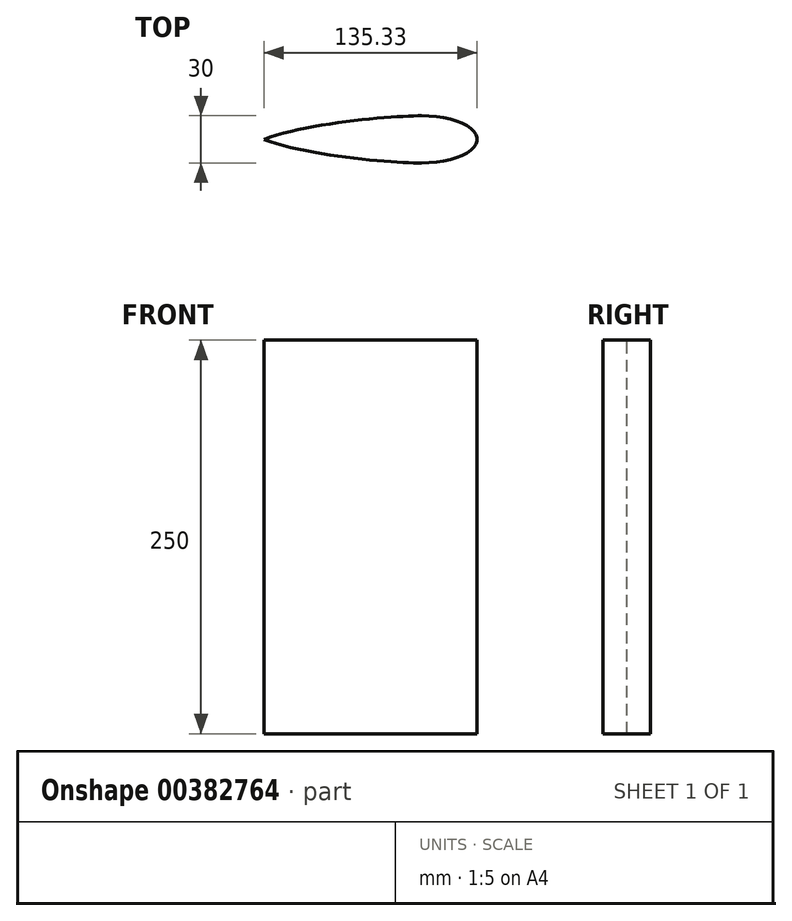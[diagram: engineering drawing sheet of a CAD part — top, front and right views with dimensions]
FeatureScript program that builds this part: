
annotation { "Feature Type Name" : "Feature", "Feature Type Description" : "" }
export const myFeature = defineFeature(function(context is Context, id is Id, definition is map)
    precondition{}
    {
        {
            var Q0;
            Q0=qCreatedBy(makeId("Top.planeOp"),FACE);
            var sketch = newSketch(context, id + "F0", { "sketchPlane" : qUnion([Q0])});
            skPoint(sketch, "E0", {"position": v(-100, 0) * mm});
            skFitSpline(sketch, "E1", {"points": [v(0, 15) * mm, v(-100, 0) * mm], "startDerivative": vector(-48.7, 0) * mm, "endDerivative": vector(-85.27, -32.97) * mm});
            skFitSpline(sketch, "E2.MirrorCS", {"points": [v(0, -15) * mm, v(-100, 0) * mm], "startDerivative": vector(-48.7, 0) * mm, "endDerivative": vector(-85.27, 32.97) * mm});
            skEllipticalArc(sketch, "E3", {});
            skLineSegment(sketch, "E4", {"start": v(-35.33, 0) * mm, "end": v(-35.33, 0) * mm});
            skLineSegment(sketch, "E5", {"start": v(0, 15) * mm, "end": v(0, 15) * mm});
            const initialGuessF0  = {"E3": [0, 0, 0, 1, 0.015, 0.03533193841576576, 3.141592653589793, 6.283185307179586]};
            skSetInitialGuess(sketch, initialGuessF0);
            skSolve(sketch);
        }
        {
            var Q0;
            Q0=makeQuery(id+"F0.imprint","IMPRINT",FACE,{"disambiguationData":[TD([[makeQuery(id+"F0.imprint","IMPRINT",EDGE,{"derivedFrom":sQuery(id+"F0.wireOp",EDGE,"E1")}),1.0]])]});
            extrude(context, id + "F1", {"entities" : qUnion([Q0]), "oppositeDirection" : true, "depth" : 250 * mm});
        }
    });
